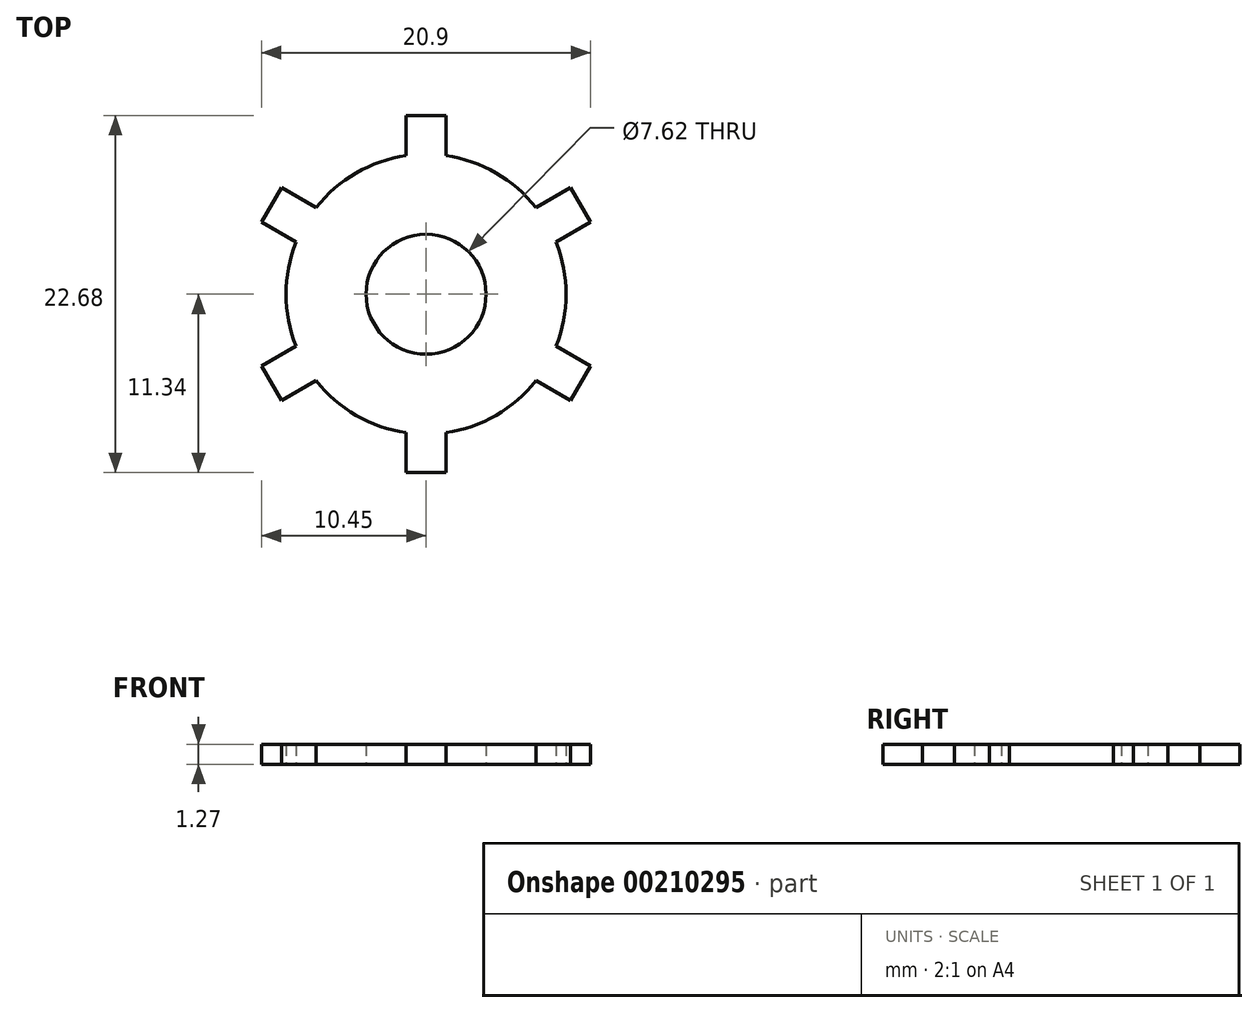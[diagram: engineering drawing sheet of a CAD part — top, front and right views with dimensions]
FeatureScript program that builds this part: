
annotation { "Feature Type Name" : "Feature", "Feature Type Description" : "" }
export const myFeature = defineFeature(function(context is Context, id is Id, definition is map)
    precondition{}
    {
        {
            var Q0;
            Q0=qCreatedBy(makeId("Top.planeOp"),FACE);
            var sketch = newSketch(context, id + "F0", { "sketchPlane" : qUnion([Q0])});
            skCircle(sketch, "E0", {"center": v(0, 0) * mm, "radius": 8.9 * mm});
            skCircle(sketch, "E1", {"center": v(0, 0) * mm, "radius": 3.81 * mm});
            skLineSegment(sketch, "E2", {"start": v(-1.27, 8.8) * mm, "end": v(-1.27, 11.34) * mm});
            skLineSegment(sketch, "E3", {"start": v(-1.27, 11.34) * mm, "end": v(1.27, 11.34) * mm});
            skLineSegment(sketch, "E4", {"start": v(1.27, 11.34) * mm, "end": v(1.27, 8.8) * mm});
            skLineSegment(sketch, "E5.1.0", {"start": v(-6.98, -5.5) * mm, "end": v(-9.18, -6.77) * mm});
            skLineSegment(sketch, "E5.1.1", {"start": v(-9.18, -6.77) * mm, "end": v(-10.45, -4.57) * mm});
            skLineSegment(sketch, "E5.1.2", {"start": v(-10.45, -4.57) * mm, "end": v(-8.26, -3.3) * mm});
            skLineSegment(sketch, "E5.2.0", {"start": v(8.25, -3.3) * mm, "end": v(10.45, -4.57) * mm});
            skLineSegment(sketch, "E5.2.1", {"start": v(10.45, -4.57) * mm, "end": v(9.18, -6.77) * mm});
            skLineSegment(sketch, "E5.2.2", {"start": v(9.18, -6.77) * mm, "end": v(6.98, -5.5) * mm});
            skLineSegment(sketch, "E6", {"start": v(-1.27, -8.8) * mm, "end": v(-1.27, -11.34) * mm});
            skLineSegment(sketch, "E7", {"start": v(-1.27, -11.34) * mm, "end": v(1.27, -11.34) * mm});
            skLineSegment(sketch, "E8", {"start": v(1.27, -11.34) * mm, "end": v(1.27, -8.8) * mm});
            skLineSegment(sketch, "E9.1.0", {"start": v(8.26, 3.3) * mm, "end": v(10.45, 4.57) * mm});
            skLineSegment(sketch, "E9.1.1", {"start": v(10.45, 4.57) * mm, "end": v(9.18, 6.77) * mm});
            skLineSegment(sketch, "E9.1.2", {"start": v(9.18, 6.77) * mm, "end": v(6.98, 5.5) * mm});
            skLineSegment(sketch, "E9.2.0", {"start": v(-6.98, 5.5) * mm, "end": v(-9.18, 6.77) * mm});
            skLineSegment(sketch, "E9.2.1", {"start": v(-9.18, 6.77) * mm, "end": v(-10.45, 4.57) * mm});
            skLineSegment(sketch, "E9.2.2", {"start": v(-10.45, 4.57) * mm, "end": v(-8.25, 3.3) * mm});
            skSolve(sketch);
        }
        {
            var Q0;
            Q0=makeQuery(id+"F0.imprint","IMPRINT",FACE,{"disambiguationData":[TD([[makeQuery(id+"F0.imprint","IMPRINT",EDGE,{"derivedFrom":sQuery(id+"F0.wireOp",EDGE,"E1")}),-1.0]])]});
            var Q1;
            {var subQ0=sQuery(id+"F0.wireOp",EDGE,"E2");Q1=makeQuery(id+"F0.imprint","IMPRINT",FACE,{"disambiguationData":[TD([[makeQuery(id+"F0.imprint","IMPRINT",EDGE,{"derivedFrom":subQ0}),-1.0]])]});}
            var Q2;
            {var subQ0=sQuery(id+"F0.wireOp",EDGE,"E9.1.0");Q2=makeQuery(id+"F0.imprint","IMPRINT",FACE,{"disambiguationData":[TD([[makeQuery(id+"F0.imprint","IMPRINT",EDGE,{"derivedFrom":subQ0}),1.0]])]});}
            var Q3;
            {var subQ0=sQuery(id+"F0.wireOp",EDGE,"E5.2.0");Q3=makeQuery(id+"F0.imprint","IMPRINT",FACE,{"disambiguationData":[TD([[makeQuery(id+"F0.imprint","IMPRINT",EDGE,{"derivedFrom":subQ0}),-1.0]])]});}
            var Q4;
            {var subQ0=sQuery(id+"F0.wireOp",EDGE,"E6");Q4=makeQuery(id+"F0.imprint","IMPRINT",FACE,{"disambiguationData":[TD([[makeQuery(id+"F0.imprint","IMPRINT",EDGE,{"derivedFrom":subQ0}),1.0]])]});}
            var Q5;
            {var subQ0=sQuery(id+"F0.wireOp",EDGE,"E5.1.0");Q5=makeQuery(id+"F0.imprint","IMPRINT",FACE,{"disambiguationData":[TD([[makeQuery(id+"F0.imprint","IMPRINT",EDGE,{"derivedFrom":subQ0}),-1.0]])]});}
            var Q6;
            {var subQ0=sQuery(id+"F0.wireOp",EDGE,"E9.2.0");Q6=makeQuery(id+"F0.imprint","IMPRINT",FACE,{"disambiguationData":[TD([[makeQuery(id+"F0.imprint","IMPRINT",EDGE,{"derivedFrom":subQ0}),1.0]])]});}
            extrude(context, id + "F1", {"entities" : qUnion([Q0, Q1, Q2, Q3, Q4, Q5, Q6]), "depth" : 1.27 * mm});
        }
    });
